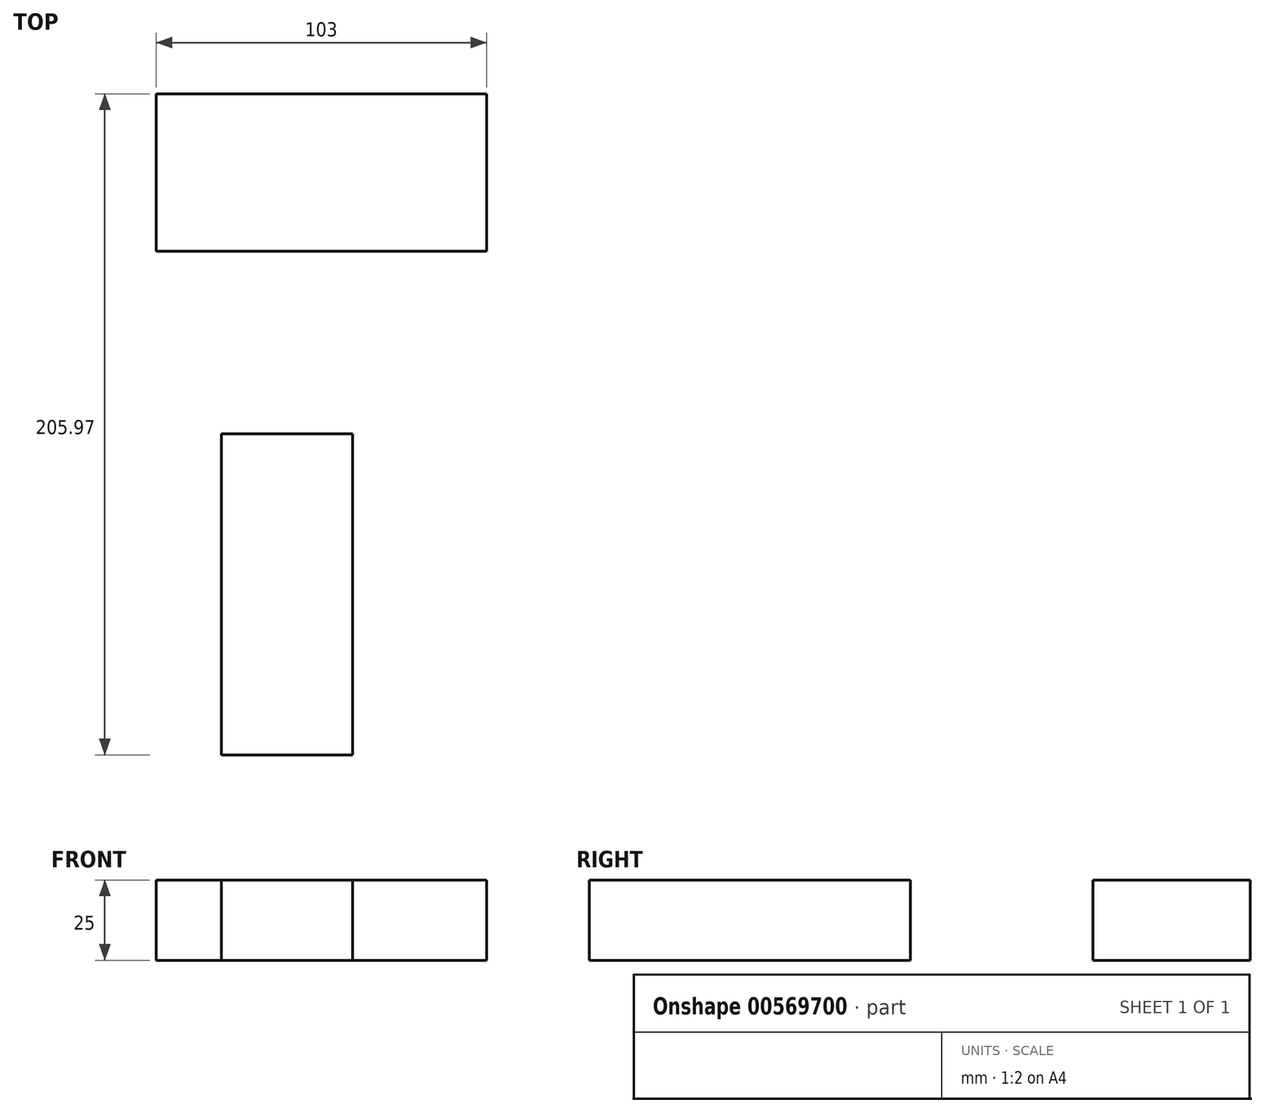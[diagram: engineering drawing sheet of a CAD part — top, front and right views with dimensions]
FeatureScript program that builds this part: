
annotation { "Feature Type Name" : "Feature", "Feature Type Description" : "" }
export const myFeature = defineFeature(function(context is Context, id is Id, definition is map)
    precondition{}
    {
        {
            var Q0;
            Q0=qCreatedBy(makeId("Top.planeOp"),FACE);
            var sketch = newSketch(context, id + "F0", { "sketchPlane" : qUnion([Q0])});
            skLineSegment(sketch, "E0.bottom", {"start": v(199.53, 165.92) * mm, "end": v(96.53, 165.92) * mm});
            skLineSegment(sketch, "E0.top", {"start": v(199.53, 116.92) * mm, "end": v(96.53, 116.92) * mm});
            skLineSegment(sketch, "E0.left", {"start": v(199.53, 165.92) * mm, "end": v(199.53, 116.92) * mm});
            skLineSegment(sketch, "E0.right", {"start": v(96.53, 165.92) * mm, "end": v(96.53, 116.92) * mm});
            skSolve(sketch);
        }
        {
            var Q0;
            Q0=qCreatedBy(makeId("Top.planeOp"),FACE);
            var sketch = newSketch(context, id + "F1", { "sketchPlane" : qUnion([Q0])});
            skLineSegment(sketch, "E1.bottom", {"start": v(157.8, 59.95) * mm, "end": v(116.8, 59.95) * mm});
            skLineSegment(sketch, "E1.top", {"start": v(157.8, -40.05) * mm, "end": v(116.8, -40.05) * mm});
            skLineSegment(sketch, "E1.left", {"start": v(157.8, 59.95) * mm, "end": v(157.8, -40.05) * mm});
            skLineSegment(sketch, "E1.right", {"start": v(116.8, 59.95) * mm, "end": v(116.8, -40.05) * mm});
            skSolve(sketch);
        }
        {
            var Q0;
            Q0 = qSketchRegion(id + "F0", true);
            extrude(context, id + "F2", {"entities" : qUnion([Q0]), "depth" : 25 * mm, "offsetDistance" : 25 * mm});
        }
        {
            var Q0;
            Q0 = qSketchRegion(id + "F1", true);
            extrude(context, id + "F3", {"entities" : qUnion([Q0]), "depth" : 25 * mm, "offsetDistance" : 25 * mm});
        }
    });
